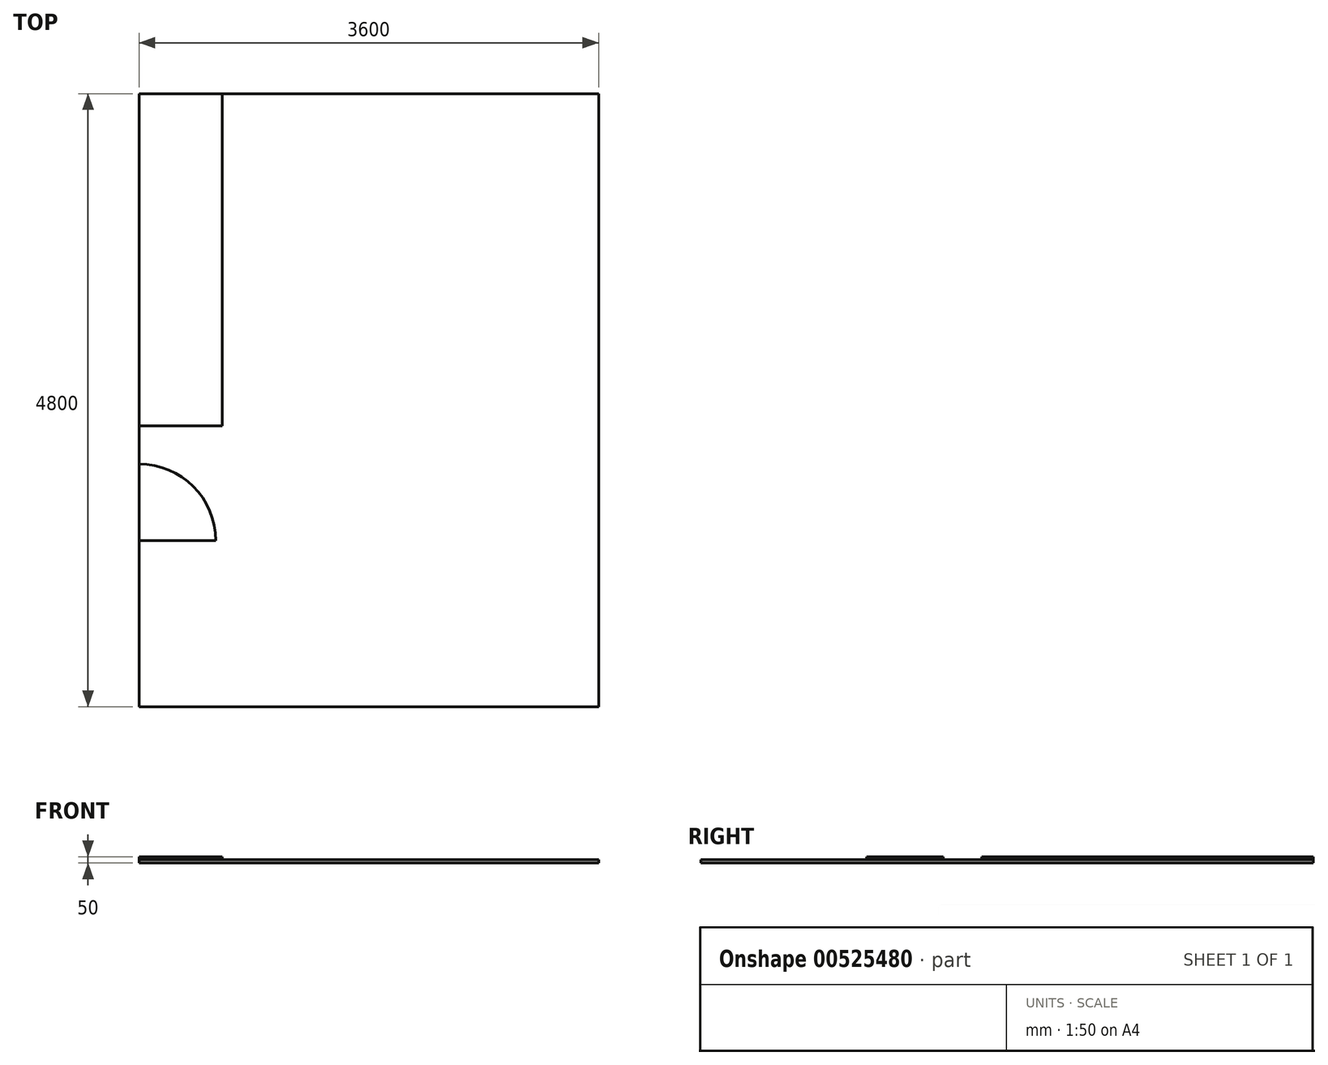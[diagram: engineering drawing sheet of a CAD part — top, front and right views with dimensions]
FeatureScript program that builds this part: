
annotation { "Feature Type Name" : "Feature", "Feature Type Description" : "" }
export const myFeature = defineFeature(function(context is Context, id is Id, definition is map)
    precondition{}
    {
        {
            var Q0;
            Q0=qCreatedBy(makeId("Top.planeOp"),FACE);
            var sketch = newSketch(context, id + "F0", { "sketchPlane" : qUnion([Q0])});
            skLineSegment(sketch, "E0.bottom", {"start": v(0, 0) * mm, "end": v(-3600, 0) * mm});
            skLineSegment(sketch, "E0.top", {"start": v(0, 4800) * mm, "end": v(-3600, 4800) * mm});
            skLineSegment(sketch, "E0.left", {"start": v(0, 0) * mm, "end": v(0, 4800) * mm});
            skLineSegment(sketch, "E0.right", {"start": v(-3600, 0) * mm, "end": v(-3600, 4800) * mm});
            skLineSegment(sketch, "E1", {"start": v(-2950, 4800) * mm, "end": v(-2950, 2200) * mm});
            skLineSegment(sketch, "E2", {"start": v(-2950, 2200) * mm, "end": v(-3600, 2200) * mm});
            skLineSegment(sketch, "E3", {"start": v(-3600, 1300) * mm, "end": v(-3000, 1300) * mm});
            skArc(sketch, "E4", {"start": v(-3000, 1300) * mm, "mid": v(-3175.74, 1724.26) * mm, "end": v(-3600, 1900) * mm});
            skSolve(sketch);
        }
        {
            var Q0;
            {var subQ3=sQuery(id+"F0.wireOp",EDGE,"E1");Q0=makeQuery(id+"F0.imprint","IMPRINT",FACE,{"disambiguationData":[TD([[makeQuery(id+"F0.imprint","IMPRINT",EDGE,{"derivedFrom":subQ3}),-1.0]])]});}
            var Q1;
            {var subQ0=sQuery(id+"F0.wireOp",EDGE,"E3");Q1=makeQuery(id+"F0.imprint","IMPRINT",FACE,{"disambiguationData":[TD([[makeQuery(id+"F0.imprint","IMPRINT",EDGE,{"derivedFrom":subQ0}),1.0]])]});}
            var Q2;
            {var subQ1=sQuery(id+"F0.wireOp",EDGE,"E0.bottom");Q2=makeQuery(id+"F0.imprint","IMPRINT",FACE,{"disambiguationData":[TD([[makeQuery(id+"F0.imprint","IMPRINT",EDGE,{"derivedFrom":subQ1}),-1.0]])]});}
            extrude(context, id + "F1", {"entities" : qUnion([Q0, Q1, Q2]), "depth" : 25 * mm, "offsetDistance" : 25 * mm});
        }
        {
            var Q0;
            Q0=makeQuery(id+"F1.opExtrude","CAP_FACE",FACE,{"disambiguationData":[OSD([sQuery(id+"F0.wireOp",EDGE,"E0.bottom"),sQuery(id+"F0.wireOp",EDGE,"E0.top"),sQuery(id+"F0.wireOp",EDGE,"E0.left"),sQuery(id+"F0.wireOp",EDGE,"E0.right")])],"isStart":false});
            var sketch = newSketch(context, id + "F2", { "sketchPlane" : qUnion([Q0])});
            skLineSegment(sketch, "E5.0", {"start": v(-2950, 4800) * mm, "end": v(-2950, 2200) * mm});
            skLineSegment(sketch, "E6.0", {"start": v(-2950, 2200) * mm, "end": v(-3600, 2200) * mm});
            skLineSegment(sketch, "E7.0", {"start": v(-3600, 1300) * mm, "end": v(-3000, 1300) * mm});
            skArc(sketch, "E8.0", {"start": v(-3000, 1300) * mm, "mid": v(-3175.74, 1724.26) * mm, "end": v(-3600, 1900) * mm});
            skLineSegment(sketch, "E9", {"start": v(-3600, 1300) * mm, "end": v(-3600, 1900) * mm});
            skLineSegment(sketch, "E10", {"start": v(-3600, 2200) * mm, "end": v(-3600, 4800) * mm});
            skLineSegment(sketch, "E11", {"start": v(-3600, 4800) * mm, "end": v(-2950, 4800) * mm});
            skSolve(sketch);
        }
        {
            var Q0;
            Q0=makeQuery(id+"F2.imprint","IMPRINT",FACE,{"disambiguationData":[TD([[makeQuery(id+"F2.imprint","IMPRINT",EDGE,{"derivedFrom":sQuery(id+"F2.wireOp",EDGE,"E5.0")}),-1.0]])]});
            var Q1;
            Q1=makeQuery(id+"F2.imprint","IMPRINT",FACE,{"disambiguationData":[TD([[makeQuery(id+"F2.imprint","IMPRINT",EDGE,{"derivedFrom":sQuery(id+"F2.wireOp",EDGE,"E7.0")}),1.0]])]});
            extrude(context, id + "F3", {"entities" : qUnion([Q0, Q1]), "operationType" : NewBodyOperationType.ADD, "depth" : 25 * mm, "offsetDistance" : 25 * mm});
        }
    });
